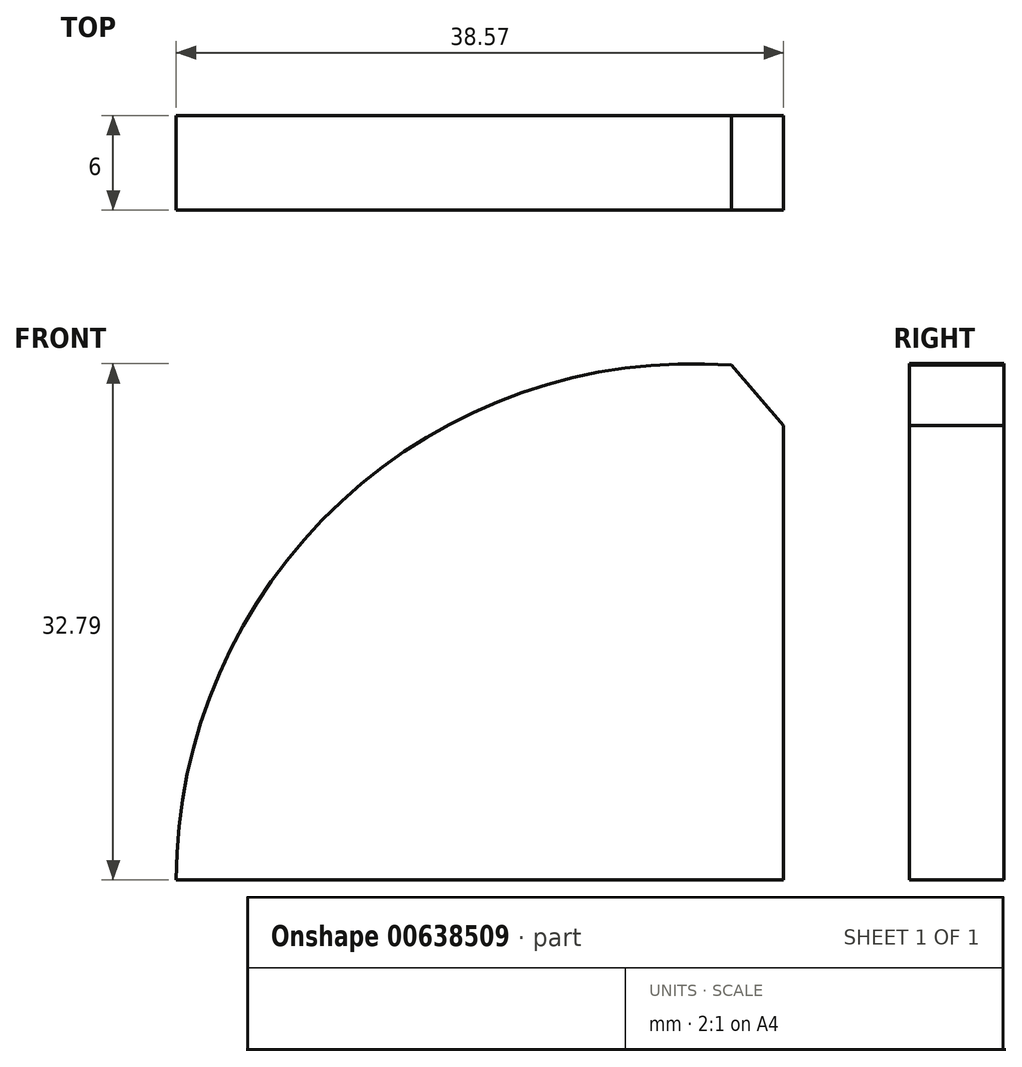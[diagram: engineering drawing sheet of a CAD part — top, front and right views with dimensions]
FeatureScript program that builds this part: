
annotation { "Feature Type Name" : "Feature", "Feature Type Description" : "" }
export const myFeature = defineFeature(function(context is Context, id is Id, definition is map)
    precondition{}
    {
        {
            var Q0;
            Q0=qCreatedBy(makeId("Front.planeOp"),FACE);
            var sketch = newSketch(context, id + "F0", { "sketchPlane" : qUnion([Q0])});
            skArc(sketch, "E0", {"start": v(-24.89, 28.85) * mm, "mid": v(-34.64, 15.87) * mm, "end": v(-38.1, 0) * mm, "construction": true});
            skArc(sketch, "E1", {"start": v(-28.2, 32.7) * mm, "mid": v(-39.26, 17.98) * mm, "end": v(-43.18, 0) * mm, "construction": true});
            skLineSegment(sketch, "E2", {"start": v(-28.2, 32.7) * mm, "end": v(0, 0) * mm, "construction": true});
            skLineSegment(sketch, "E3", {"start": v(-28.2, 32.7) * mm, "end": v(-24.89, 28.85) * mm});
            skLineSegment(sketch, "E4", {"start": v(-38.1, 0) * mm, "end": v(-63.46, 0) * mm});
            skArc(sketch, "E5", {"start": v(-28.2, 32.7) * mm, "mid": v(-52.97, 24.04) * mm, "end": v(-63.46, 0) * mm});
            skLineSegment(sketch, "E6", {"start": v(-38.1, 0) * mm, "end": v(0, 0) * mm, "construction": true});
            skLineSegment(sketch, "E7", {"start": v(-24.89, 28.85) * mm, "end": v(-24.89, 0) * mm});
            skLineSegment(sketch, "E8", {"start": v(-24.89, 0) * mm, "end": v(-38.1, 0) * mm});
            skSolve(sketch);
        }
        {
            var Q0;
            Q0 = qSketchRegion(id + "F0", true);
            extrude(context, id + "F1", {"entities" : qUnion([Q0]), "depth" : 3 * mm, "offsetDistance" : 25.4 * mm});
        }
        {
            var Q0;
            Q0 = qSketchRegion(id + "F0", true);
            extrude(context, id + "F2", {"entities" : qUnion([Q0]), "operationType" : NewBodyOperationType.ADD, "oppositeDirection" : true, "depth" : 3 * mm, "offsetDistance" : 25.4 * mm});
        }
    });
